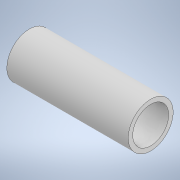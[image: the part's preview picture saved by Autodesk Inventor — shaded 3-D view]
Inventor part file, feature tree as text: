
AUTODESK INVENTOR PART (.ipt)
format: ipt  version: 2021 (Build 250183000, 183)  size: 96,768 bytes
history: native  units: mm
features: extrude x1, sketch x1
ambient origin geometry x8: Origin, YZ Plane, XZ Plane, XY Plane, X Axis, Y Axis, Z Axis, Center Point
bodies: Solid1 (feature_tree)
feature tree (2):
  extrude  "Extrusion1"  Depth=100.0mm TaperAngle=0.0deg
  sketch  "Sketch1"  dims[d0=37.0mm d1=100.0mm d2=0.0mm d3=0.5mm d4=0.872665mm]
